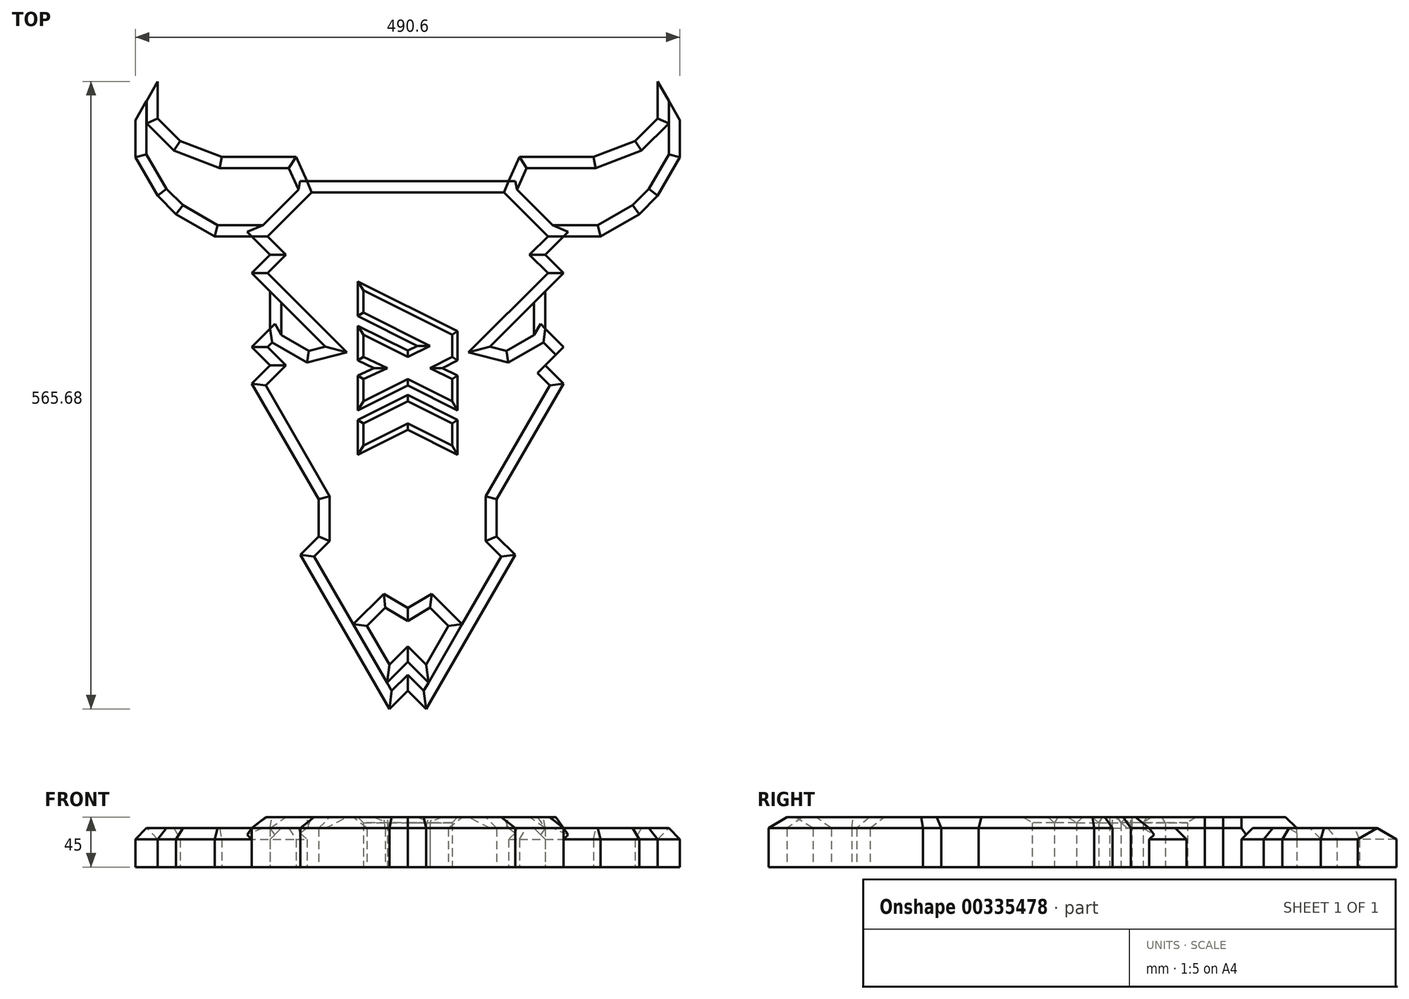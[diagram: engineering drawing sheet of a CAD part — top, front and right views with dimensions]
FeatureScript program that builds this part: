
annotation { "Feature Type Name" : "Feature", "Feature Type Description" : "" }
export const myFeature = defineFeature(function(context is Context, id is Id, definition is map)
    precondition{}
    {
        {
            var Q0;
            Q0=qCreatedBy(makeId("Top.planeOp"),FACE);
            var sketch = newSketch(context, id + "F0", { "sketchPlane" : qUnion([Q0])});
            skLineSegment(sketch, "E0", {"start": v(0, 0) * mm, "end": v(-16.56, -16.56) * mm});
            skLineSegment(sketch, "E1", {"start": v(-16.56, -16.56) * mm, "end": v(-36.62, 18.2) * mm});
            skLineSegment(sketch, "E2", {"start": v(-36.62, 18.2) * mm, "end": v(-20.07, 34.76) * mm});
            skLineSegment(sketch, "E3", {"start": v(-20.07, 34.76) * mm, "end": v(0, 22.7) * mm});
            skLineSegment(sketch, "E4", {"start": v(0, -40) * mm, "end": v(-16.56, -56.56) * mm});
            skLineSegment(sketch, "E5", {"start": v(-16.56, -56.56) * mm, "end": v(-96.83, 82.48) * mm});
            skLineSegment(sketch, "E6", {"start": v(-96.83, 82.48) * mm, "end": v(-80.27, 99.03) * mm});
            skLineSegment(sketch, "E7", {"start": v(-80.27, 99.03) * mm, "end": v(-80.27, 132.48) * mm});
            skLineSegment(sketch, "E8", {"start": v(-80.27, 132.48) * mm, "end": v(-140.48, 236.76) * mm});
            skLineSegment(sketch, "E9", {"start": v(-140.48, 236.76) * mm, "end": v(-123.92, 253.31) * mm});
            skLineSegment(sketch, "E10", {"start": v(-123.92, 253.31) * mm, "end": v(-107.36, 236.76) * mm});
            skLineSegment(sketch, "E11", {"start": v(-107.36, 236.76) * mm, "end": v(-140.48, 269.87) * mm});
            skLineSegment(sketch, "E12", {"start": v(-140.48, 269.87) * mm, "end": v(-123.92, 286.42) * mm});
            skLineSegment(sketch, "E13", {"start": v(-123.92, 286.42) * mm, "end": v(-123.92, 319.87) * mm});
            skLineSegment(sketch, "E14", {"start": v(-123.92, 319.87) * mm, "end": v(-140.48, 336.42) * mm});
            skLineSegment(sketch, "E15", {"start": v(-140.48, 336.42) * mm, "end": v(-74.25, 270.2) * mm});
            skLineSegment(sketch, "E16", {"start": v(-123.92, 286.42) * mm, "end": v(-89.16, 266.35) * mm});
            skLineSegment(sketch, "E17", {"start": v(-89.16, 266.35) * mm, "end": v(-74.25, 270.2) * mm});
            skLineSegment(sketch, "E18", {"start": v(-140.48, 336.42) * mm, "end": v(-107.36, 369.53) * mm});
            skPoint(sketch, "E19", {"position": v(-123.92, 352.98) * mm});
            skLineSegment(sketch, "E20", {"start": v(-123.92, 352.98) * mm, "end": v(-140.48, 369.53) * mm});
            skLineSegment(sketch, "E21", {"start": v(-140.48, 369.53) * mm, "end": v(-90.8, 419.2) * mm});
            skLineSegment(sketch, "E22", {"start": v(-90.8, 419.2) * mm, "end": v(0, 419.2) * mm});
            skLineSegment(sketch, "E23", {"start": v(-140.48, 369.53) * mm, "end": v(-173.92, 369.53) * mm});
            skLineSegment(sketch, "E24", {"start": v(-173.92, 369.53) * mm, "end": v(-208.68, 389.6) * mm});
            skLineSegment(sketch, "E25", {"start": v(-208.68, 389.6) * mm, "end": v(-225.24, 406.16) * mm});
            skLineSegment(sketch, "E26", {"start": v(-225.24, 406.16) * mm, "end": v(-245.3, 440.92) * mm});
            skLineSegment(sketch, "E27", {"start": v(-245.3, 440.92) * mm, "end": v(-245.3, 474.36) * mm});
            skLineSegment(sketch, "E28", {"start": v(-245.3, 474.36) * mm, "end": v(-225.24, 509.12) * mm});
            skLineSegment(sketch, "E29", {"start": v(-225.24, 509.12) * mm, "end": v(-225.24, 475.67) * mm});
            skLineSegment(sketch, "E30", {"start": v(-225.24, 475.67) * mm, "end": v(-205.04, 455.48) * mm});
            skLineSegment(sketch, "E31", {"start": v(-205.04, 455.48) * mm, "end": v(-167.54, 441.16) * mm});
            skLineSegment(sketch, "E32", {"start": v(-167.54, 441.16) * mm, "end": v(-100.65, 441.16) * mm});
            skLineSegment(sketch, "E33", {"start": v(-100.65, 441.16) * mm, "end": v(-90.8, 419.2) * mm});
            skLineSegment(sketch, "E34.MirrorCS", {"start": v(123.92, 253.31) * mm, "end": v(107.36, 236.76) * mm});
            skLineSegment(sketch, "E35.MirrorCS", {"start": v(140.48, 269.87) * mm, "end": v(123.92, 286.42) * mm});
            skLineSegment(sketch, "E36.MirrorCS", {"start": v(89.16, 266.35) * mm, "end": v(74.25, 270.2) * mm});
            skLineSegment(sketch, "E37.MirrorCS", {"start": v(123.92, 352.98) * mm, "end": v(140.48, 369.53) * mm});
            skLineSegment(sketch, "E38.MirrorCS", {"start": v(208.68, 389.6) * mm, "end": v(225.24, 406.16) * mm});
            skLineSegment(sketch, "E39.MirrorCS", {"start": v(225.24, 475.67) * mm, "end": v(205.04, 455.48) * mm});
            skLineSegment(sketch, "E40.MirrorCS", {"start": v(0, -40) * mm, "end": v(16.56, -56.56) * mm});
            skLineSegment(sketch, "E41.MirrorCS", {"start": v(96.83, 82.48) * mm, "end": v(80.27, 99.03) * mm});
            skLineSegment(sketch, "E42.MirrorCS", {"start": v(107.36, 236.76) * mm, "end": v(140.48, 269.87) * mm});
            skLineSegment(sketch, "E43.MirrorCS", {"start": v(36.62, 18.2) * mm, "end": v(20.07, 34.76) * mm});
            skLineSegment(sketch, "E44.MirrorCS", {"start": v(140.48, 236.76) * mm, "end": v(123.92, 253.31) * mm});
            skLineSegment(sketch, "E45.MirrorCS", {"start": v(123.92, 319.87) * mm, "end": v(140.48, 336.42) * mm});
            skLineSegment(sketch, "E46.MirrorCS", {"start": v(100.65, 441.16) * mm, "end": v(90.8, 419.2) * mm});
            skLineSegment(sketch, "E47.MirrorCS", {"start": v(140.48, 336.42) * mm, "end": v(74.25, 270.2) * mm});
            skLineSegment(sketch, "E48.MirrorCS", {"start": v(225.24, 509.12) * mm, "end": v(225.24, 475.67) * mm});
            skLineSegment(sketch, "E49.MirrorCS", {"start": v(140.48, 369.53) * mm, "end": v(173.92, 369.53) * mm});
            skLineSegment(sketch, "E50.MirrorCS", {"start": v(225.24, 406.16) * mm, "end": v(245.3, 440.92) * mm});
            skLineSegment(sketch, "E51.MirrorCS", {"start": v(173.92, 369.53) * mm, "end": v(208.68, 389.6) * mm});
            skLineSegment(sketch, "E52.MirrorCS", {"start": v(245.3, 440.92) * mm, "end": v(245.3, 474.36) * mm});
            skLineSegment(sketch, "E53.MirrorCS", {"start": v(140.48, 336.42) * mm, "end": v(107.36, 369.53) * mm});
            skLineSegment(sketch, "E54.MirrorCS", {"start": v(20.07, 34.76) * mm, "end": v(0, 22.7) * mm});
            skLineSegment(sketch, "E55.MirrorCS", {"start": v(123.92, 286.42) * mm, "end": v(89.16, 266.35) * mm});
            skLineSegment(sketch, "E56.MirrorCS", {"start": v(123.92, 286.42) * mm, "end": v(123.92, 319.87) * mm});
            skLineSegment(sketch, "E57.MirrorCS", {"start": v(16.56, -16.56) * mm, "end": v(36.62, 18.2) * mm});
            skLineSegment(sketch, "E58.MirrorCS", {"start": v(0, 0) * mm, "end": v(16.56, -16.56) * mm});
            skLineSegment(sketch, "E59.MirrorCS", {"start": v(167.54, 441.16) * mm, "end": v(100.65, 441.16) * mm});
            skLineSegment(sketch, "E60.MirrorCS", {"start": v(205.04, 455.48) * mm, "end": v(167.54, 441.16) * mm});
            skLineSegment(sketch, "E61.MirrorCS", {"start": v(245.3, 474.36) * mm, "end": v(225.24, 509.12) * mm});
            skLineSegment(sketch, "E62.MirrorCS", {"start": v(140.48, 369.53) * mm, "end": v(90.8, 419.2) * mm});
            skLineSegment(sketch, "E63.MirrorCS", {"start": v(90.8, 419.2) * mm, "end": v(0, 419.2) * mm});
            skLineSegment(sketch, "E64.MirrorCS", {"start": v(16.56, -56.56) * mm, "end": v(96.83, 82.48) * mm});
            skLineSegment(sketch, "E65.MirrorCS", {"start": v(80.27, 132.48) * mm, "end": v(140.48, 236.76) * mm});
            skLineSegment(sketch, "E66.MirrorCS", {"start": v(80.27, 99.03) * mm, "end": v(80.27, 132.48) * mm});
            skPoint(sketch, "E67.MirrorP", {"position": v(123.92, 352.98) * mm});
            skLineSegment(sketch, "E68", {"start": v(-40, 320.85) * mm, "end": v(40, 280.85) * mm});
            skLineSegment(sketch, "E69", {"start": v(-40, 320.85) * mm, "end": v(-40, 300.85) * mm});
            skLineSegment(sketch, "E70", {"start": v(-40, 300.85) * mm, "end": v(20, 270.85) * mm});
            skLineSegment(sketch, "E71", {"start": v(-40, 240.85) * mm, "end": v(-40, 220.85) * mm});
            skLineSegment(sketch, "E72", {"start": v(40, 260.85) * mm, "end": v(40, 280.85) * mm});
            skPoint(sketch, "E73", {"position": v(40, 270.85) * mm});
            skLineSegment(sketch, "E74", {"start": v(-40, 280.85) * mm, "end": v(-40, 260.85) * mm});
            skLineSegment(sketch, "E75", {"start": v(40, 240.85) * mm, "end": v(40, 220.85) * mm});
            skPoint(sketch, "E76", {"position": v(0, 260.85) * mm});
            skPoint(sketch, "E77", {"position": v(-18.26, 250.85) * mm});
            skPoint(sketch, "E78", {"position": v(20, 250.85) * mm});
            skPoint(sketch, "E79", {"position": v(0, 240.85) * mm});
            skLineSegment(sketch, "E80", {"start": v(0, 240.85) * mm, "end": v(40, 220.85) * mm});
            skLineSegment(sketch, "E81", {"start": v(0, 240.85) * mm, "end": v(-40, 220.85) * mm});
            skPoint(sketch, "E82", {"position": v(0, 220.85) * mm});
            skLineSegment(sketch, "E83", {"start": v(0, 260.85) * mm, "end": v(20, 270.85) * mm});
            skLineSegment(sketch, "E84", {"start": v(20, 250.85) * mm, "end": v(40, 260.85) * mm});
            skLineSegment(sketch, "E85", {"start": v(-40, 260.85) * mm, "end": v(-18.26, 250.85) * mm});
            skLineSegment(sketch, "E86", {"start": v(-40, 280.85) * mm, "end": v(0, 260.85) * mm});
            skLineSegment(sketch, "E87", {"start": v(-40, 240.85) * mm, "end": v(-18.26, 250.85) * mm});
            skLineSegment(sketch, "E88", {"start": v(20, 250.85) * mm, "end": v(40, 240.85) * mm});
            skPoint(sketch, "E89", {"position": v(0, 300.85) * mm});
            skLineSegment(sketch, "E90", {"start": v(-40, 200.85) * mm, "end": v(-40, 180.85) * mm});
            skLineSegment(sketch, "E91", {"start": v(40, 200.85) * mm, "end": v(40, 180.85) * mm});
            skPoint(sketch, "E92", {"position": v(0, 200.85) * mm});
            skLineSegment(sketch, "E93", {"start": v(0, 220.85) * mm, "end": v(40, 200.85) * mm});
            skLineSegment(sketch, "E94", {"start": v(0, 200.85) * mm, "end": v(40, 180.85) * mm});
            skLineSegment(sketch, "E95", {"start": v(0, 200.85) * mm, "end": v(-40, 180.85) * mm});
            skLineSegment(sketch, "E96", {"start": v(-40, 200.85) * mm, "end": v(0, 220.85) * mm});
            skSolve(sketch);
        }
        {
            var Q0;
            Q0=makeQuery(id+"F0.imprint","IMPRINT",FACE,{"disambiguationData":[TD([[makeQuery(id+"F0.imprint","IMPRINT",EDGE,{"derivedFrom":sQuery(id+"F0.wireOp",EDGE,"E0")}),1.0]])]});
            extrude(context, id + "F1", {"entities" : qUnion([Q0]), "depth" : 15 * mm, "hasSecondDirection" : true, "secondDirectionOppositeDirection" : true, "secondDirectionDepth" : 30 * mm});
        }
        {
            var Q0;
            Q0=makeQuery(id+"F0.imprint","IMPRINT",FACE,{"disambiguationData":[TD([[makeQuery(id+"F0.imprint","IMPRINT",EDGE,{"derivedFrom":sQuery(id+"F0.wireOp",EDGE,"E21")}),1.0]])]});
            var Q1;
            Q1=makeQuery(id+"F0.imprint","IMPRINT",FACE,{"disambiguationData":[TD([[makeQuery(id+"F0.imprint","IMPRINT",EDGE,{"derivedFrom":sQuery(id+"F0.wireOp",EDGE,"E38.MirrorCS")}),1.0]])]});
            extrude(context, id + "F2", {"entities" : qUnion([Q0, Q1]), "operationType" : NewBodyOperationType.ADD, "depth" : 5 * mm, "hasSecondDirection" : true, "secondDirectionOppositeDirection" : true, "secondDirectionDepth" : 30 * mm});
        }
        {
            var Q0;
            {var subQ0=sQuery(id+"F0.wireOp",EDGE,"E13");Q0=makeQuery(id+"F0.imprint","IMPRINT",FACE,{"disambiguationData":[TD([[makeQuery(id+"F0.imprint","IMPRINT",EDGE,{"derivedFrom":subQ0}),-1.0]])]});}
            var Q1;
            {var subQ0=sQuery(id+"F0.wireOp",EDGE,"E36.MirrorCS");Q1=makeQuery(id+"F0.imprint","IMPRINT",FACE,{"disambiguationData":[TD([[makeQuery(id+"F0.imprint","IMPRINT",EDGE,{"derivedFrom":subQ0}),-1.0]])]});}
            extrude(context, id + "F3", {"entities" : qUnion([Q0, Q1]), "operationType" : NewBodyOperationType.ADD, "depth" : 5 * mm, "hasSecondDirection" : true, "secondDirectionOppositeDirection" : true, "secondDirectionDepth" : 30 * mm});
        }
        {
            var Q0;
            Q0=makeQuery(id+"F1.opExtrude","CAP_EDGE",EDGE,{"disambiguationData":[OSD([sQuery(id+"F0.wireOp",EDGE,"E8")])],"isStart":false});
            var Q1;
            Q1=makeQuery(id+"F1.opExtrude","CAP_EDGE",EDGE,{"disambiguationData":[OSD([sQuery(id+"F0.wireOp",EDGE,"E7")])],"isStart":false});
            var Q2;
            Q2=makeQuery(id+"F1.opExtrude","CAP_EDGE",EDGE,{"disambiguationData":[OSD([sQuery(id+"F0.wireOp",EDGE,"E6")])],"isStart":false});
            var Q3;
            Q3=makeQuery(id+"F1.opExtrude","CAP_EDGE",EDGE,{"disambiguationData":[OSD([sQuery(id+"F0.wireOp",EDGE,"E5")])],"isStart":false});
            var Q4;
            Q4=makeQuery(id+"F1.opExtrude","CAP_EDGE",EDGE,{"disambiguationData":[OSD([sQuery(id+"F0.wireOp",EDGE,"E2")])],"isStart":false});
            var Q5;
            Q5=makeQuery(id+"F1.opExtrude","CAP_EDGE",EDGE,{"disambiguationData":[OSD([sQuery(id+"F0.wireOp",EDGE,"E1")])],"isStart":false});
            var Q6;
            Q6=makeQuery(id+"F1.opExtrude","CAP_EDGE",EDGE,{"disambiguationData":[OSD([sQuery(id+"F0.wireOp",EDGE,"E3")])],"isStart":false});
            var Q7;
            Q7=makeQuery(id+"F1.opExtrude","CAP_EDGE",EDGE,{"disambiguationData":[OSD([sQuery(id+"F0.wireOp",EDGE,"E54.MirrorCS")])],"isStart":false});
            var Q8;
            Q8=makeQuery(id+"F1.opExtrude","CAP_EDGE",EDGE,{"disambiguationData":[OSD([sQuery(id+"F0.wireOp",EDGE,"E43.MirrorCS")])],"isStart":false});
            var Q9;
            Q9=makeQuery(id+"F1.opExtrude","CAP_EDGE",EDGE,{"disambiguationData":[OSD([sQuery(id+"F0.wireOp",EDGE,"E57.MirrorCS")])],"isStart":false});
            var Q10;
            Q10=makeQuery(id+"F1.opExtrude","CAP_EDGE",EDGE,{"disambiguationData":[OSD([sQuery(id+"F0.wireOp",EDGE,"E58.MirrorCS")])],"isStart":false});
            var Q11;
            Q11=makeQuery(id+"F1.opExtrude","CAP_EDGE",EDGE,{"disambiguationData":[OSD([sQuery(id+"F0.wireOp",EDGE,"E0")])],"isStart":false});
            var Q12;
            Q12=makeQuery(id+"F1.opExtrude","CAP_EDGE",EDGE,{"disambiguationData":[OSD([sQuery(id+"F0.wireOp",EDGE,"E4")])],"isStart":false});
            var Q13;
            Q13=makeQuery(id+"F1.opExtrude","CAP_EDGE",EDGE,{"disambiguationData":[OSD([sQuery(id+"F0.wireOp",EDGE,"E40.MirrorCS")])],"isStart":false});
            var Q14;
            Q14=makeQuery(id+"F1.opExtrude","CAP_EDGE",EDGE,{"disambiguationData":[OSD([sQuery(id+"F0.wireOp",EDGE,"E64.MirrorCS")])],"isStart":false});
            var Q15;
            Q15=makeQuery(id+"F1.opExtrude","CAP_EDGE",EDGE,{"disambiguationData":[OSD([sQuery(id+"F0.wireOp",EDGE,"E66.MirrorCS")])],"isStart":false});
            var Q16;
            Q16=makeQuery(id+"F1.opExtrude","CAP_EDGE",EDGE,{"disambiguationData":[OSD([sQuery(id+"F0.wireOp",EDGE,"E41.MirrorCS")])],"isStart":false});
            var Q17;
            Q17=makeQuery(id+"F1.opExtrude","CAP_EDGE",EDGE,{"disambiguationData":[OSD([sQuery(id+"F0.wireOp",EDGE,"E65.MirrorCS")])],"isStart":false});
            var Q18;
            Q18=makeQuery(id+"F1.opExtrude","CAP_EDGE",EDGE,{"disambiguationData":[OSD([sQuery(id+"F0.wireOp",EDGE,"E9")])],"isStart":false});
            var Q19;
            Q19=makeQuery(id+"F1.opExtrude","CAP_EDGE",EDGE,{"disambiguationData":[OSD([sQuery(id+"F0.wireOp",EDGE,"E12")])],"isStart":false});
            var Q20;
            Q20=makeQuery(id+"F1.opExtrude","CAP_EDGE",EDGE,{"disambiguationData":[OSD([sQuery(id+"F0.wireOp",EDGE,"E11")])],"isStart":false});
            var Q21;
            Q21=makeQuery(id+"F1.opExtrude","CAP_EDGE",EDGE,{"disambiguationData":[OSD([sQuery(id+"F0.wireOp",EDGE,"E16")])],"isStart":false});
            var Q22;
            Q22=makeQuery(id+"F1.opExtrude","CAP_EDGE",EDGE,{"disambiguationData":[OSD([sQuery(id+"F0.wireOp",EDGE,"E15")])],"isStart":false});
            var Q23;
            Q23=makeQuery(id+"F1.opExtrude","CAP_EDGE",EDGE,{"disambiguationData":[OSD([sQuery(id+"F0.wireOp",EDGE,"E17")])],"isStart":false});
            var Q24;
            Q24=makeQuery(id+"F1.opExtrude","CAP_EDGE",EDGE,{"disambiguationData":[OSD([sQuery(id+"F0.wireOp",EDGE,"E36.MirrorCS")])],"isStart":false});
            var Q25;
            Q25=makeQuery(id+"F1.opExtrude","CAP_EDGE",EDGE,{"disambiguationData":[OSD([sQuery(id+"F0.wireOp",EDGE,"E55.MirrorCS")])],"isStart":false});
            var Q26;
            Q26=makeQuery(id+"F1.opExtrude","CAP_EDGE",EDGE,{"disambiguationData":[OSD([sQuery(id+"F0.wireOp",EDGE,"E35.MirrorCS")])],"isStart":false});
            var Q27;
            Q27=makeQuery(id+"F1.opExtrude","CAP_EDGE",EDGE,{"disambiguationData":[OSD([sQuery(id+"F0.wireOp",EDGE,"E44.MirrorCS")])],"isStart":false});
            var Q28;
            Q28=makeQuery(id+"F1.opExtrude","CAP_EDGE",EDGE,{"disambiguationData":[OSD([sQuery(id+"F0.wireOp",EDGE,"E47.MirrorCS")])],"isStart":false});
            var Q29;
            Q29=makeQuery(id+"F1.opExtrude","CAP_EDGE",EDGE,{"disambiguationData":[OSD([sQuery(id+"F0.wireOp",EDGE,"E53.MirrorCS")])],"isStart":false});
            var Q30;
            Q30=makeQuery(id+"F1.opExtrude","CAP_EDGE",EDGE,{"disambiguationData":[OSD([sQuery(id+"F0.wireOp",EDGE,"E37.MirrorCS")])],"isStart":false});
            var Q31;
            Q31=makeQuery(id+"F1.opExtrude","CAP_EDGE",EDGE,{"disambiguationData":[OSD([sQuery(id+"F0.wireOp",EDGE,"E62.MirrorCS")])],"isStart":false});
            var Q32;
            Q32=makeQuery(id+"F1.opExtrude","CAP_EDGE",EDGE,{"disambiguationData":[OSD([sQuery(id+"F0.wireOp",EDGE,"E22"),sQuery(id+"F0.wireOp",EDGE,"E63.MirrorCS")])],"isStart":false});
            var Q33;
            Q33=makeQuery(id+"F1.opExtrude","CAP_EDGE",EDGE,{"disambiguationData":[OSD([sQuery(id+"F0.wireOp",EDGE,"E21")])],"isStart":false});
            var Q34;
            Q34=makeQuery(id+"F1.opExtrude","CAP_EDGE",EDGE,{"disambiguationData":[OSD([sQuery(id+"F0.wireOp",EDGE,"E20")])],"isStart":false});
            var Q35;
            Q35=makeQuery(id+"F1.opExtrude","CAP_EDGE",EDGE,{"disambiguationData":[OSD([sQuery(id+"F0.wireOp",EDGE,"E18")])],"isStart":false});
            chamfer(context, id + "F4", {"entities" : qUnion([Q0, Q1, Q2, Q3, Q4, Q5, Q6, Q7, Q8, Q9, Q10, Q11, Q12, Q13, Q14, Q15, Q16, Q17, Q18, Q19, Q20, Q21, Q22, Q23, Q24, Q25, Q26, Q27, Q28, Q29, Q30, Q31, Q32, Q33, Q34, Q35]), "width" : 10 * mm, "tangentPropagation" : true});
        }
        {
            var Q0;
            Q0=makeQuery(id+"F2.opExtrude","CAP_EDGE",EDGE,{"disambiguationData":[OSD([sQuery(id+"F0.wireOp",EDGE,"E33")])],"isStart":false});
            var Q1;
            Q1=makeQuery(id+"F2.opExtrude","CAP_EDGE",EDGE,{"disambiguationData":[OSD([sQuery(id+"F0.wireOp",EDGE,"E32")])],"isStart":false});
            var Q2;
            Q2=makeQuery(id+"F2.opExtrude","CAP_EDGE",EDGE,{"disambiguationData":[OSD([sQuery(id+"F0.wireOp",EDGE,"E31")])],"isStart":false});
            var Q3;
            Q3=makeQuery(id+"F2.opExtrude","CAP_EDGE",EDGE,{"disambiguationData":[OSD([sQuery(id+"F0.wireOp",EDGE,"E30")])],"isStart":false});
            var Q4;
            Q4=makeQuery(id+"F2.opExtrude","CAP_EDGE",EDGE,{"disambiguationData":[OSD([sQuery(id+"F0.wireOp",EDGE,"E27")])],"isStart":false});
            var Q5;
            Q5=makeQuery(id+"F2.opExtrude","CAP_EDGE",EDGE,{"disambiguationData":[OSD([sQuery(id+"F0.wireOp",EDGE,"E26")])],"isStart":false});
            var Q6;
            Q6=makeQuery(id+"F2.opExtrude","CAP_EDGE",EDGE,{"disambiguationData":[OSD([sQuery(id+"F0.wireOp",EDGE,"E25")])],"isStart":false});
            var Q7;
            Q7=makeQuery(id+"F2.opExtrude","CAP_EDGE",EDGE,{"disambiguationData":[OSD([sQuery(id+"F0.wireOp",EDGE,"E24")])],"isStart":false});
            var Q8;
            Q8=makeQuery(id+"F2.opExtrude","CAP_EDGE",EDGE,{"disambiguationData":[OSD([sQuery(id+"F0.wireOp",EDGE,"E23")])],"isStart":false});
            var Q9;
            Q9=makeQuery(id+"F2.opExtrude","CAP_EDGE",EDGE,{"disambiguationData":[OSD([sQuery(id+"F0.wireOp",EDGE,"E29")])],"isStart":false});
            var Q10;
            Q10=makeQuery(id+"F2.opExtrude","CAP_EDGE",EDGE,{"disambiguationData":[OSD([sQuery(id+"F0.wireOp",EDGE,"E59.MirrorCS")])],"isStart":false});
            var Q11;
            Q11=makeQuery(id+"F2.opExtrude","CAP_EDGE",EDGE,{"disambiguationData":[OSD([sQuery(id+"F0.wireOp",EDGE,"E46.MirrorCS")])],"isStart":false});
            var Q12;
            Q12=makeQuery(id+"F2.opExtrude","CAP_EDGE",EDGE,{"disambiguationData":[OSD([sQuery(id+"F0.wireOp",EDGE,"E49.MirrorCS")])],"isStart":false});
            var Q13;
            Q13=makeQuery(id+"F2.opExtrude","CAP_EDGE",EDGE,{"disambiguationData":[OSD([sQuery(id+"F0.wireOp",EDGE,"E51.MirrorCS")])],"isStart":false});
            var Q14;
            Q14=makeQuery(id+"F2.opExtrude","CAP_EDGE",EDGE,{"disambiguationData":[OSD([sQuery(id+"F0.wireOp",EDGE,"E38.MirrorCS")])],"isStart":false});
            var Q15;
            Q15=makeQuery(id+"F2.opExtrude","CAP_EDGE",EDGE,{"disambiguationData":[OSD([sQuery(id+"F0.wireOp",EDGE,"E50.MirrorCS")])],"isStart":false});
            var Q16;
            Q16=makeQuery(id+"F2.opExtrude","CAP_EDGE",EDGE,{"disambiguationData":[OSD([sQuery(id+"F0.wireOp",EDGE,"E60.MirrorCS")])],"isStart":false});
            var Q17;
            Q17=makeQuery(id+"F2.opExtrude","CAP_EDGE",EDGE,{"disambiguationData":[OSD([sQuery(id+"F0.wireOp",EDGE,"E39.MirrorCS")])],"isStart":false});
            var Q18;
            Q18=makeQuery(id+"F2.opExtrude","CAP_EDGE",EDGE,{"disambiguationData":[OSD([sQuery(id+"F0.wireOp",EDGE,"E48.MirrorCS")])],"isStart":false});
            var Q19;
            Q19=makeQuery(id+"F2.opExtrude","CAP_EDGE",EDGE,{"disambiguationData":[OSD([sQuery(id+"F0.wireOp",EDGE,"E52.MirrorCS")])],"isStart":false});
            chamfer(context, id + "F5", {"entities" : qUnion([Q0, Q1, Q2, Q3, Q4, Q5, Q6, Q7, Q8, Q9, Q10, Q11, Q12, Q13, Q14, Q15, Q16, Q17, Q18, Q19]), "width" : 10 * mm, "tangentPropagation" : true});
        }
        {
            var Q0;
            Q0=makeQuery(id+"F1.opExtrude","CAP_EDGE",EDGE,{"disambiguationData":[OSD([sQuery(id+"F0.wireOp",EDGE,"E81")])],"isStart":false});
            var Q1;
            Q1=makeQuery(id+"F1.opExtrude","CAP_EDGE",EDGE,{"disambiguationData":[OSD([sQuery(id+"F0.wireOp",EDGE,"E71")])],"isStart":false});
            var Q2;
            Q2=makeQuery(id+"F1.opExtrude","CAP_EDGE",EDGE,{"disambiguationData":[OSD([sQuery(id+"F0.wireOp",EDGE,"E87")])],"isStart":false});
            var Q3;
            Q3=makeQuery(id+"F1.opExtrude","CAP_EDGE",EDGE,{"disambiguationData":[OSD([sQuery(id+"F0.wireOp",EDGE,"E85")])],"isStart":false});
            var Q4;
            Q4=makeQuery(id+"F1.opExtrude","CAP_EDGE",EDGE,{"disambiguationData":[OSD([sQuery(id+"F0.wireOp",EDGE,"E74")])],"isStart":false});
            var Q5;
            Q5=makeQuery(id+"F1.opExtrude","CAP_EDGE",EDGE,{"disambiguationData":[OSD([sQuery(id+"F0.wireOp",EDGE,"E86")])],"isStart":false});
            var Q6;
            Q6=makeQuery(id+"F1.opExtrude","CAP_EDGE",EDGE,{"disambiguationData":[OSD([sQuery(id+"F0.wireOp",EDGE,"E83")])],"isStart":false});
            var Q7;
            Q7=makeQuery(id+"F1.opExtrude","CAP_EDGE",EDGE,{"disambiguationData":[OSD([sQuery(id+"F0.wireOp",EDGE,"E70")])],"isStart":false});
            var Q8;
            Q8=makeQuery(id+"F1.opExtrude","CAP_EDGE",EDGE,{"disambiguationData":[OSD([sQuery(id+"F0.wireOp",EDGE,"E69")])],"isStart":false});
            var Q9;
            Q9=makeQuery(id+"F1.opExtrude","CAP_EDGE",EDGE,{"disambiguationData":[OSD([sQuery(id+"F0.wireOp",EDGE,"E68")])],"isStart":false});
            var Q10;
            Q10=makeQuery(id+"F1.opExtrude","CAP_EDGE",EDGE,{"disambiguationData":[OSD([sQuery(id+"F0.wireOp",EDGE,"E84")])],"isStart":false});
            var Q11;
            Q11=makeQuery(id+"F1.opExtrude","CAP_EDGE",EDGE,{"disambiguationData":[OSD([sQuery(id+"F0.wireOp",EDGE,"E72")])],"isStart":false});
            var Q12;
            Q12=makeQuery(id+"F1.opExtrude","CAP_EDGE",EDGE,{"disambiguationData":[OSD([sQuery(id+"F0.wireOp",EDGE,"E88")])],"isStart":false});
            var Q13;
            Q13=makeQuery(id+"F1.opExtrude","CAP_EDGE",EDGE,{"disambiguationData":[OSD([sQuery(id+"F0.wireOp",EDGE,"E75")])],"isStart":false});
            var Q14;
            Q14=makeQuery(id+"F1.opExtrude","CAP_EDGE",EDGE,{"disambiguationData":[OSD([sQuery(id+"F0.wireOp",EDGE,"E80")])],"isStart":false});
            var Q15;
            Q15=makeQuery(id+"F1.opExtrude","CAP_EDGE",EDGE,{"disambiguationData":[OSD([sQuery(id+"F0.wireOp",EDGE,"E93")])],"isStart":false});
            var Q16;
            Q16=makeQuery(id+"F1.opExtrude","CAP_EDGE",EDGE,{"disambiguationData":[OSD([sQuery(id+"F0.wireOp",EDGE,"E96")])],"isStart":false});
            var Q17;
            Q17=makeQuery(id+"F1.opExtrude","CAP_EDGE",EDGE,{"disambiguationData":[OSD([sQuery(id+"F0.wireOp",EDGE,"E90")])],"isStart":false});
            var Q18;
            Q18=makeQuery(id+"F1.opExtrude","CAP_EDGE",EDGE,{"disambiguationData":[OSD([sQuery(id+"F0.wireOp",EDGE,"E95")])],"isStart":false});
            var Q19;
            Q19=makeQuery(id+"F1.opExtrude","CAP_EDGE",EDGE,{"disambiguationData":[OSD([sQuery(id+"F0.wireOp",EDGE,"E94")])],"isStart":false});
            var Q20;
            Q20=makeQuery(id+"F1.opExtrude","CAP_EDGE",EDGE,{"disambiguationData":[OSD([sQuery(id+"F0.wireOp",EDGE,"E91")])],"isStart":false});
            chamfer(context, id + "F6", {"entities" : qUnion([Q0, Q1, Q2, Q3, Q4, Q5, Q6, Q7, Q8, Q9, Q10, Q11, Q12, Q13, Q14, Q15, Q16, Q17, Q18, Q19, Q20]), "width" : 5 * mm, "tangentPropagation" : true});
        }
        {
            var Q0;
            Q0=makeQuery(id+"F3.opExtrude","CAP_EDGE",EDGE,{"disambiguationData":[OSD([sQuery(id+"F0.wireOp",EDGE,"E56.MirrorCS")])],"isStart":false});
            var Q1;
            Q1=makeQuery(id+"F3.opExtrude","CAP_EDGE",EDGE,{"disambiguationData":[OSD([sQuery(id+"F0.wireOp",EDGE,"E13")])],"isStart":false});
            chamfer(context, id + "F7", {"entities" : qUnion([Q0, Q1]), "width" : 10 * mm, "tangentPropagation" : true});
        }
    });
